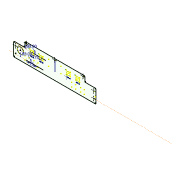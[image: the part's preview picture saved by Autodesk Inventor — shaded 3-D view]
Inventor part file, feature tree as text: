
AUTODESK INVENTOR PART (.ipt)
format: ipt  version: 2017 (Build 210142000, 142)  size: 387,072 bytes
history: native  units: in
note: dims shown in document units (in); Inventor stores cm internally (conversion verified against a paired STEP export)
features: reference x22, sketch x15, extrude x11, other x5, pattern_linear x3, hole x2, projected_geometry x1
ambient origin geometry x8: Origin, YZ Plane, XZ Plane, XY Plane, X Axis, Y Axis, Z Axis, Center Point
bodies: Solid1 (feature_tree)
feature tree (59):
  sketch  "Sketch2"  dims[d9=0.1181in d10=0.0in d11=0.1181in d12=0.0in]
  sketch  "Sketch3"  dims[d13=180.0deg d14=180.0deg]
  extrude  "Extrusion1"  Depth=0.1181in TaperAngle=0.0deg
  extrude  "Extrusion2"  TaperAngle=180.0deg  [1 undecoded]
  sketch  "Sketch5"  dims[d25=0.126in d26=0.126in]
  sketch  "Sketch6"  dims[d27=0.126in d28=0.126in]
  sketch  "Sketch7"  dims[d29=0.126in d30=0.126in]
  extrude  "Extrusion3"  Depth=2.9528in
  sketch  "Sketch9"  dims[d32=0.126in]
  hole  "Hole2"  [1 undecoded]
  hole  "Hole3"  [1 undecoded]
  sketch  "Sketch11"  dims[d42=0.1181in d43=0.2362in d44=0.1575in d45=0.0787in d46=90.0deg d47=0.315in d48=0.8108in d49=1.9685in d50=1.9685in d51=3.937in]
  extrude  "Extrusion5"  Depth=0.126in
  pattern_linear  "Rectangular Pattern1"  Count1=5  [1 undecoded]
  pattern_linear  "Rectangular Pattern2"  Count1=5  [1 undecoded]
  pattern_linear  "Rectangular Pattern3"  Count1=10  [1 undecoded]
  sketch  "Sketch14"  dims[d54=1.5748in d55=1.2224in d56=1.2224in]
  extrude  "Extrusion6"  Depth=1.2224in
  extrude  "Extrusion7"  Depth=1.2224in
  sketch  "Sketch17"  dims[d78=0.7874in d80=2.9528in d81=0.3937in d82=0.0in d83=0.3937in d84=0.0in]
  sketch  "Sketch4"  dims[d15=2.9528in d16=2.9528in]
  reference  "Reference1"
  reference  "Reference2"
  reference  "Reference3"
  reference  "Reference4"
  reference  "Reference11"
  sketch  "Sketch8"  dims[d31=0.126in]
  reference  "Reference12"
  reference  "Reference13"
  sketch  "Sketch10"  dims[d40=0.3937in d41=0.0in]
  projected_geometry  "Projected Loop1"
  sketch  "Sketch13"  dims[d52=1.2224in d53=1.2224in]
  sketch  "Sketch15"  dims[d57=0.1181in d58=0.2362in d59=0.1575in d60=0.0787in d61=90.0deg d62=0.315in d63=0.8108in d70=0.3937in d71=0.0in]
  reference  "Reference14"
  reference  "Reference15"
  reference  "Reference16"
  reference  "Reference17"
  reference  "Reference18"
  reference  "Reference19"
  reference  "Reference20"
  reference  "Reference21"
  reference  "Reference22"
  reference  "Reference23"
  reference  "Reference24"
  reference  "Reference25"
  reference  "Reference26"
  reference  "Reference27"
  sketch  "Sketch16"  dims[d72=0.7874in d74=2.9528in d75=0.7874in d77=11.5748in]
  reference  "Reference28"
  other  "<userpath>\OneDrive\Inventor\Beast 3D Printer\Extruder Assembly.iam"
  extrude  "Extruder Assembly.iam"  Depth=0.3937in TaperAngle=0.0deg
  extrude  "Extruder and Arm Sub Ass_CPY1:1"  Depth=11.5748in
  other  "Spring Block_CPY1:1"
  extrude  "Extruder Arm_CPY1:1"  Depth=0.3937in TaperAngle=0.0deg
  extrude  "Extruder and Arm Sub Ass_CPY2:1"  Depth=0.3937in TaperAngle=0.0deg
  other  "Spring Block_CPY2:1"
  extrude  "Extruder Arm_CPY2:1"  [1 undecoded]
  other  "Stepper Motor - Nema 17_CPY1:1"
  other  "Stepper Motor - Nema 17_CPY2:1"
note: 7 required parameter values undecoded (feature->parameter linkage not recoverable at this tier; creation-order binding heuristic only, values carry confidence <= 0.55)
